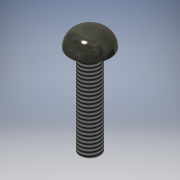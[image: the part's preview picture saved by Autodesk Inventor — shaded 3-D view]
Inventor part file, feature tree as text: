
AUTODESK INVENTOR PART (.ipt)
format: ipt  version: 2016 (Build 200138000, 138)  size: 141,824 bytes
history: native  units: mm
features: extrude x3, sketch x3, other x1, fillet x1, thread x1
ambient origin geometry x1: Origin
bodies: Body1 (feature_tree)
feature tree (9):
  other  "ソリッド1"
  extrude  "押し出し1"  Depth=4.0mm
  extrude  "押し出し2"  Depth=6.0mm TaperAngle=0.0deg
  fillet  "フィレット1"  Radius=8.0mm
  thread  "ねじ1"
  extrude  "押し出し3"  Depth=3.0mm TaperAngle=0.0deg
  sketch  "スケッチ1"
  sketch  "スケッチ2"
  sketch  "スケッチ3"
